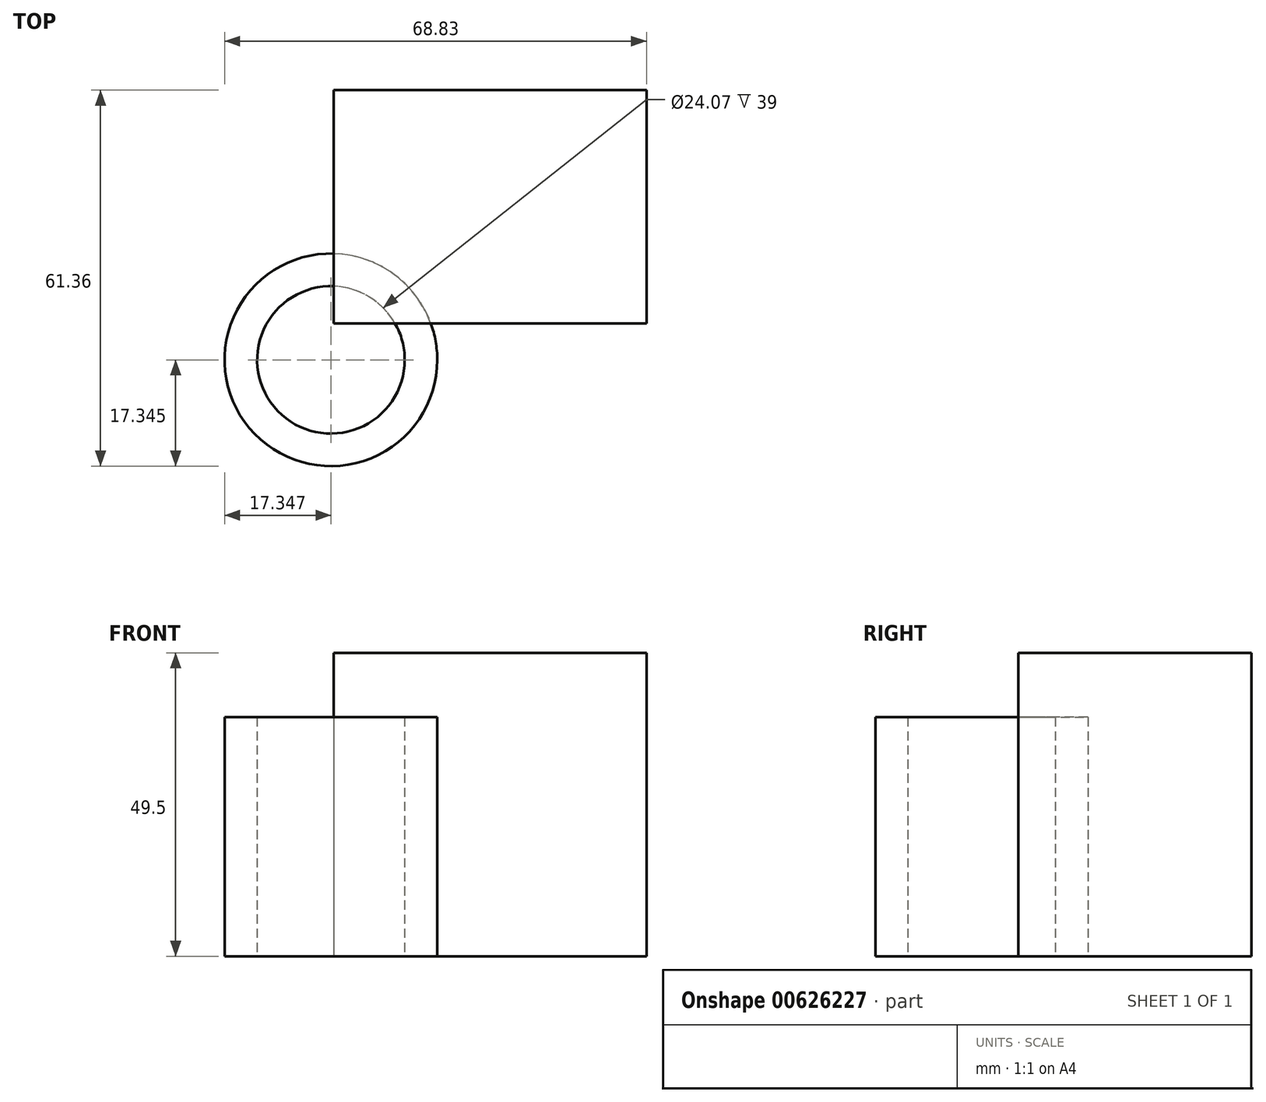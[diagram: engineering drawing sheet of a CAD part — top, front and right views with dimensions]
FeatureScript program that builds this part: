
annotation { "Feature Type Name" : "Feature", "Feature Type Description" : "" }
export const myFeature = defineFeature(function(context is Context, id is Id, definition is map)
    precondition{}
    {
        {
            var Q0;
            Q0=qCreatedBy(makeId("Top.planeOp"),FACE);
            var sketch = newSketch(context, id + "F0", { "sketchPlane" : qUnion([Q0])});
            skLineSegment(sketch, "E0.bottom", {"start": v(-85.66, 52.32) * mm, "end": v(-34.64, 52.32) * mm});
            skLineSegment(sketch, "E0.top", {"start": v(-85.66, 14.28) * mm, "end": v(-34.64, 14.28) * mm});
            skLineSegment(sketch, "E0.left", {"start": v(-85.66, 52.32) * mm, "end": v(-85.66, 14.28) * mm});
            skLineSegment(sketch, "E0.right", {"start": v(-34.64, 52.32) * mm, "end": v(-34.64, 14.28) * mm});
            skSolve(sketch);
        }
        {
            var Q0;
            Q0 = qSketchRegion(id + "F0", true);
            extrude(context, id + "F1", {"entities" : qUnion([Q0]), "depth" : 49.5 * mm, "offsetDistance" : 25 * mm});
        }
        {
            var Q0;
            Q0=qCreatedBy(makeId("Top.planeOp"),FACE);
            var sketch = newSketch(context, id + "F2", { "sketchPlane" : qUnion([Q0])});
            skCircle(sketch, "E1", {"center": v(-72.92, -17.4) * mm, "radius": 12.04 * mm});
            skCircle(sketch, "E2", {"center": v(-72.92, -17.4) * mm, "radius": 17.35 * mm});
            skSolve(sketch);
        }
        {
            var Q0;
            Q0 = qSketchRegion(id + "F2", true);
            extrude(context, id + "F3", {"entities" : qUnion([Q0]), "depth" : 39 * mm, "offsetDistance" : 25 * mm});
        }
        {
            var Q0;
            Q0=makeQuery(id+"F3.opExtrude","SWEPT_BODY",BODY,{"disambiguationData":[OSD([sQuery(id+"F2.wireOp",EDGE,"E1"),sQuery(id+"F2.wireOp",EDGE,"E2")])]});
            transform(context, id + "F4", {"entities" : qUnion([Q0]), "transformType" : TransformType.TRANSLATION_3D, "dx" : -13.2 * mm, "dy" : 25.7 * mm, "dz" : 0 * mm, "makeCopy" : false});
        }
    });
